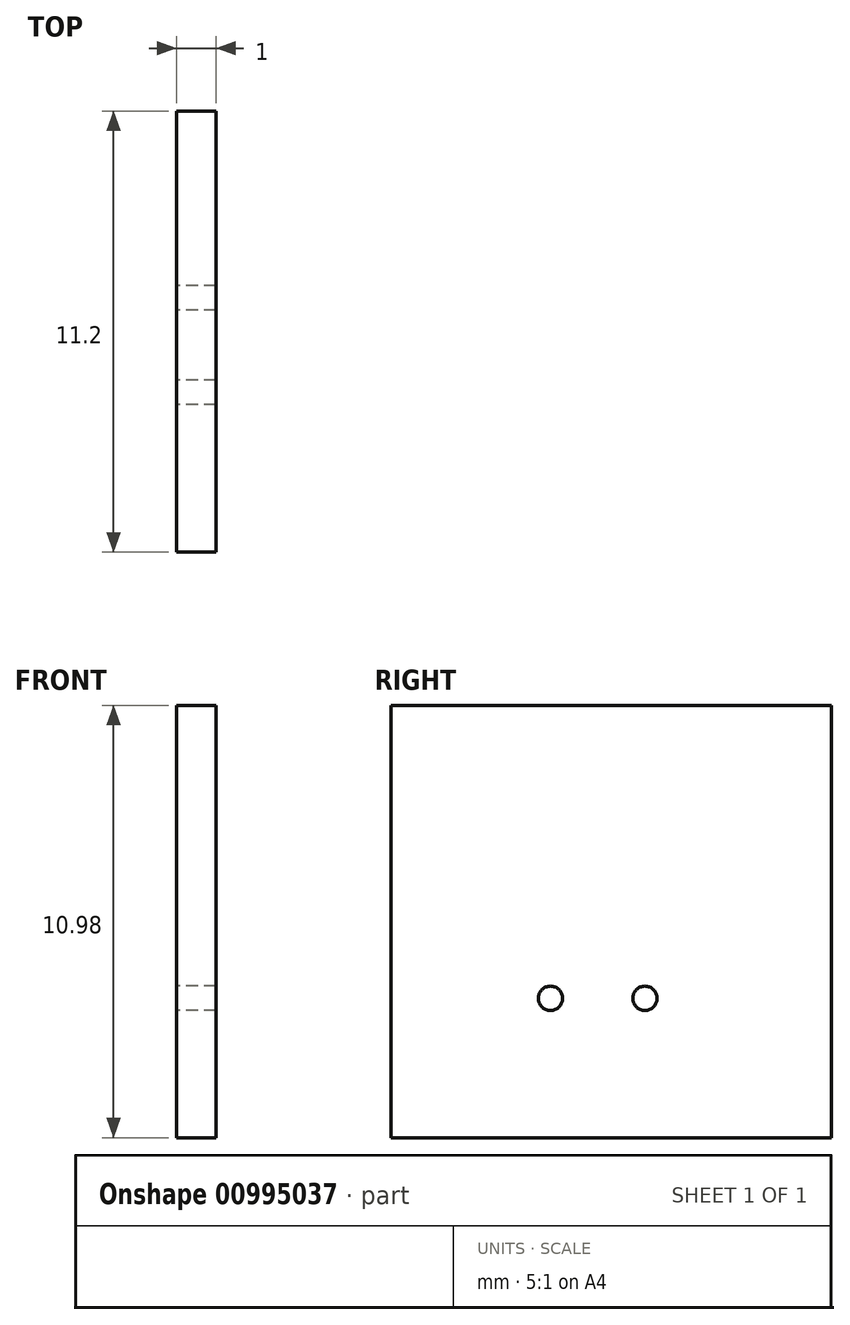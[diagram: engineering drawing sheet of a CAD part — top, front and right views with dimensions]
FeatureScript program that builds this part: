
annotation { "Feature Type Name" : "Feature", "Feature Type Description" : "" }
export const myFeature = defineFeature(function(context is Context, id is Id, definition is map)
    precondition{}
    {
        {
            var Q0;
            Q0=qCreatedBy(makeId("Right.planeOp"),FACE);
            var sketch = newSketch(context, id + "F0", { "sketchPlane" : qUnion([Q0])});
            skCircle(sketch, "E0", {"center": v(1.2, -2.7) * mm, "radius": 0.3 * mm});
            skLineSegment(sketch, "E1", {"start": v(0, -0.8) * mm, "end": v(0, -1.85) * mm, "construction": true});
            skCircle(sketch, "E2.MirrorC", {"center": v(-1.2, -2.7) * mm, "radius": 0.3 * mm});
            skLineSegment(sketch, "E3.bottom", {"start": v(5.94, 4.74) * mm, "end": v(-5.26, 4.74) * mm});
            skLineSegment(sketch, "E3.top", {"start": v(5.94, -6.24) * mm, "end": v(-5.26, -6.24) * mm});
            skLineSegment(sketch, "E3.left", {"start": v(5.94, 4.74) * mm, "end": v(5.94, -6.24) * mm});
            skLineSegment(sketch, "E3.right", {"start": v(-5.26, 4.74) * mm, "end": v(-5.26, -6.24) * mm});
            skSolve(sketch);
        }
        {
            var Q0;
            Q0=qSketchRegion(id+"F0",true);
            extrude(context, id + "F1", {"entities" : qUnion([Q0]), "depth" : 1 * mm, "offsetDistance" : 25 * mm});
        }
    });
